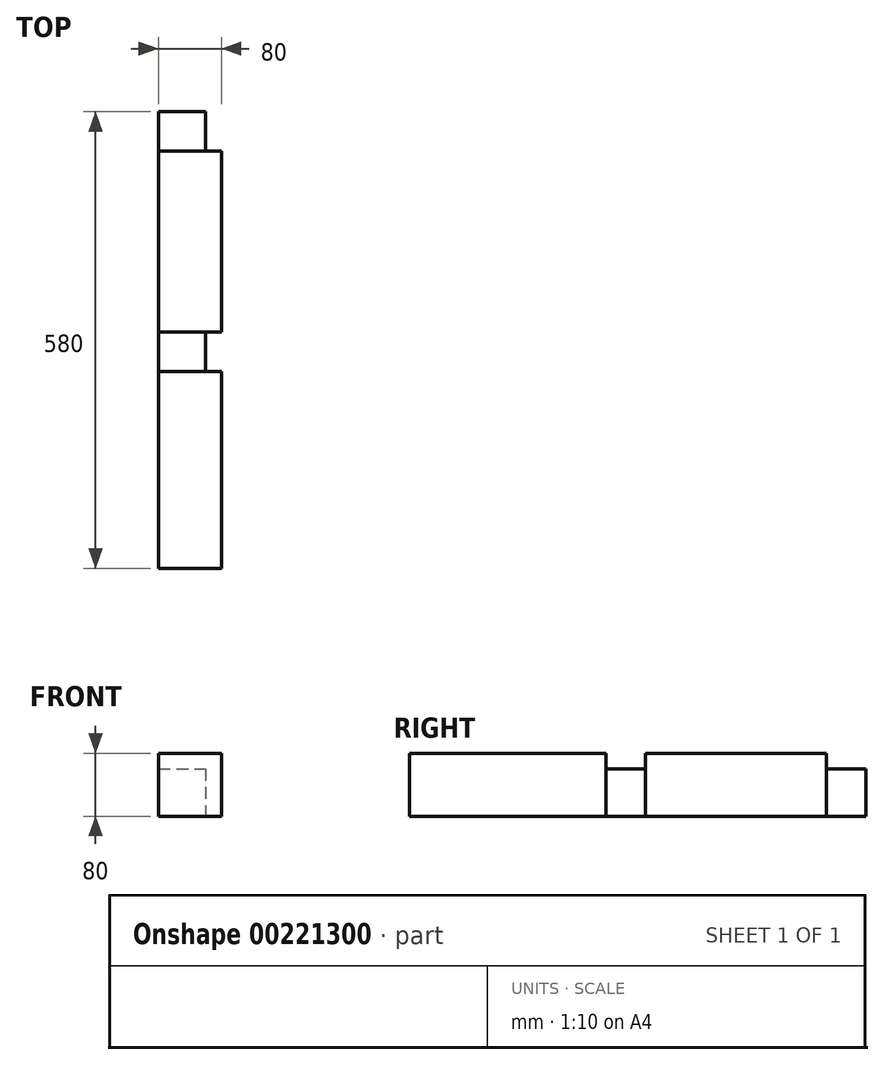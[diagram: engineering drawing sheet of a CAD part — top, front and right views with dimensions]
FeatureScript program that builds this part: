
annotation { "Feature Type Name" : "Feature", "Feature Type Description" : "" }
export const myFeature = defineFeature(function(context is Context, id is Id, definition is map)
    precondition{}
    {
        {
            var Q0;
            Q0=qCreatedBy(makeId("Front.planeOp"),FACE);
            var sketch = newSketch(context, id + "F0", { "sketchPlane" : qUnion([Q0])});
            skLineSegment(sketch, "E0.bottom", {"start": v(-35.43, 30.48) * mm, "end": v(44.57, 30.48) * mm});
            skLineSegment(sketch, "E0.top", {"start": v(-35.43, -49.52) * mm, "end": v(44.57, -49.52) * mm});
            skLineSegment(sketch, "E0.left", {"start": v(-35.43, 30.48) * mm, "end": v(-35.43, -49.52) * mm});
            skLineSegment(sketch, "E0.right", {"start": v(44.57, 30.48) * mm, "end": v(44.57, -49.52) * mm});
            skSolve(sketch);
        }
        {
            var Q0;
            Q0=makeQuery(id+"F0.imprint","IMPRINT",FACE,{"disambiguationData":[TD([[makeQuery(id+"F0.imprint","IMPRINT",EDGE,{"derivedFrom":sQuery(id+"F0.wireOp",EDGE,"E0.bottom")}),-1.0]])]});
            extrude(context, id + "F1", {"entities" : qUnion([Q0]), "oppositeDirection" : true, "depth" : 580 * mm});
        }
        {
            var Q0;
            Q0=makeQuery(id+"F1.opExtrude","SWEPT_FACE",FACE,{"disambiguationData":[OSD([sQuery(id+"F0.wireOp",EDGE,"E0.bottom")])]});
            var sketch = newSketch(context, id + "F2", { "sketchPlane" : qUnion([Q0])});
            skLineSegment(sketch, "E1.bottom", {"start": v(-35.43, 300) * mm, "end": v(44.57, 300) * mm});
            skLineSegment(sketch, "E1.top", {"start": v(-35.43, 250) * mm, "end": v(44.57, 250) * mm});
            skLineSegment(sketch, "E1.left", {"start": v(-35.43, 300) * mm, "end": v(-35.43, 250) * mm});
            skLineSegment(sketch, "E1.right", {"start": v(44.57, 300) * mm, "end": v(44.57, 250) * mm});
            skSolve(sketch);
        }
        {
            var Q0;
            Q0=makeQuery(id+"F2.imprint","IMPRINT",FACE,{"disambiguationData":[TD([[makeQuery(id+"F2.imprint","IMPRINT",EDGE,{"derivedFrom":sQuery(id+"F2.wireOp",EDGE,"E1.bottom")}),-1.0]])]});
            extrude(context, id + "F3", {"entities" : qUnion([Q0]), "operationType" : NewBodyOperationType.REMOVE, "oppositeDirection" : true, "depth" : 20 * mm});
        }
        {
            var Q0;
            Q0=makeQuery(id+"F1.opExtrude","SWEPT_FACE",FACE,{"disambiguationData":[OSD([sQuery(id+"F0.wireOp",EDGE,"E0.right")])]});
            var sketch = newSketch(context, id + "F4", { "sketchPlane" : qUnion([Q0])});
            skLineSegment(sketch, "E2.bottom", {"start": v(250, 10.48) * mm, "end": v(300, 10.48) * mm});
            skLineSegment(sketch, "E2.top", {"start": v(250, -49.52) * mm, "end": v(300, -49.52) * mm});
            skLineSegment(sketch, "E2.left", {"start": v(250, 10.48) * mm, "end": v(250, -49.52) * mm});
            skLineSegment(sketch, "E2.right", {"start": v(300, 10.48) * mm, "end": v(300, -49.52) * mm});
            skSolve(sketch);
        }
        {
            var Q0;
            Q0=makeQuery(id+"F4.imprint","IMPRINT",FACE,{"disambiguationData":[TD([[makeQuery(id+"F4.imprint","IMPRINT",EDGE,{"derivedFrom":sQuery(id+"F4.wireOp",EDGE,"E2.bottom")}),1.0]])]});
            extrude(context, id + "F5", {"entities" : qUnion([Q0]), "operationType" : NewBodyOperationType.REMOVE, "oppositeDirection" : true, "depth" : 20 * mm});
        }
        {
            var Q0;
            {var subQ2=sQuery(id+"F0.wireOp",EDGE,"E0.bottom");Q0=makeQuery(id+"F3.boolean.opBoolean","SPLIT",FACE,{"disambiguationData":[TD([makeQuery(id+"F3.opExtrude","SWEPT_FACE",FACE,{"disambiguationData":[OSD([sQuery(id+"F2.wireOp",EDGE,"E1.bottom")])]})])],"derivedFrom":makeQuery(id+"F1.opExtrude","SWEPT_FACE",FACE,{"disambiguationData":[OSD([subQ2])]})});}
            var sketch = newSketch(context, id + "F6", { "sketchPlane" : qUnion([Q0])});
            skLineSegment(sketch, "E3.bottom", {"start": v(-35.43, 580) * mm, "end": v(44.57, 580) * mm});
            skLineSegment(sketch, "E3.top", {"start": v(-35.43, 530) * mm, "end": v(44.57, 530) * mm});
            skLineSegment(sketch, "E3.left", {"start": v(-35.43, 580) * mm, "end": v(-35.43, 530) * mm});
            skLineSegment(sketch, "E3.right", {"start": v(44.57, 580) * mm, "end": v(44.57, 530) * mm});
            skSolve(sketch);
        }
        {
            var Q0;
            Q0=makeQuery(id+"F6.imprint","IMPRINT",FACE,{"disambiguationData":[TD([[makeQuery(id+"F6.imprint","IMPRINT",EDGE,{"derivedFrom":sQuery(id+"F6.wireOp",EDGE,"E3.bottom")}),-1.0]])]});
            extrude(context, id + "F7", {"entities" : qUnion([Q0]), "operationType" : NewBodyOperationType.REMOVE, "oppositeDirection" : true, "depth" : 20 * mm});
        }
        {
            var Q0;
            {var subQ1=sQuery(id+"F0.wireOp",EDGE,"E0.right");Q0=makeQuery(id+"F5.boolean.opBoolean","SPLIT",FACE,{"disambiguationData":[TD([makeQuery(id+"F3.boolean.opBoolean","COPY",FACE,{"derivedFrom":makeQuery(id+"F3.opExtrude","SWEPT_FACE",FACE,{"disambiguationData":[OSD([sQuery(id+"F2.wireOp",EDGE,"E1.bottom")])]})})])],"derivedFrom":makeQuery(id+"F1.opExtrude","SWEPT_FACE",FACE,{"disambiguationData":[OSD([subQ1])]})});}
            var sketch = newSketch(context, id + "F8", { "sketchPlane" : qUnion([Q0])});
            skLineSegment(sketch, "E4.bottom", {"start": v(530, 10.48) * mm, "end": v(580, 10.48) * mm});
            skLineSegment(sketch, "E4.top", {"start": v(530, -49.52) * mm, "end": v(580, -49.52) * mm});
            skLineSegment(sketch, "E4.left", {"start": v(530, 10.48) * mm, "end": v(530, -49.52) * mm});
            skLineSegment(sketch, "E4.right", {"start": v(580, 10.48) * mm, "end": v(580, -49.52) * mm});
            skSolve(sketch);
        }
        {
            var Q0;
            Q0=makeQuery(id+"F8.imprint","IMPRINT",FACE,{"disambiguationData":[TD([[makeQuery(id+"F8.imprint","IMPRINT",EDGE,{"derivedFrom":sQuery(id+"F8.wireOp",EDGE,"E4.bottom")}),1.0]])]});
            extrude(context, id + "F9", {"entities" : qUnion([Q0]), "operationType" : NewBodyOperationType.REMOVE, "oppositeDirection" : true, "depth" : 20 * mm});
        }
    });
